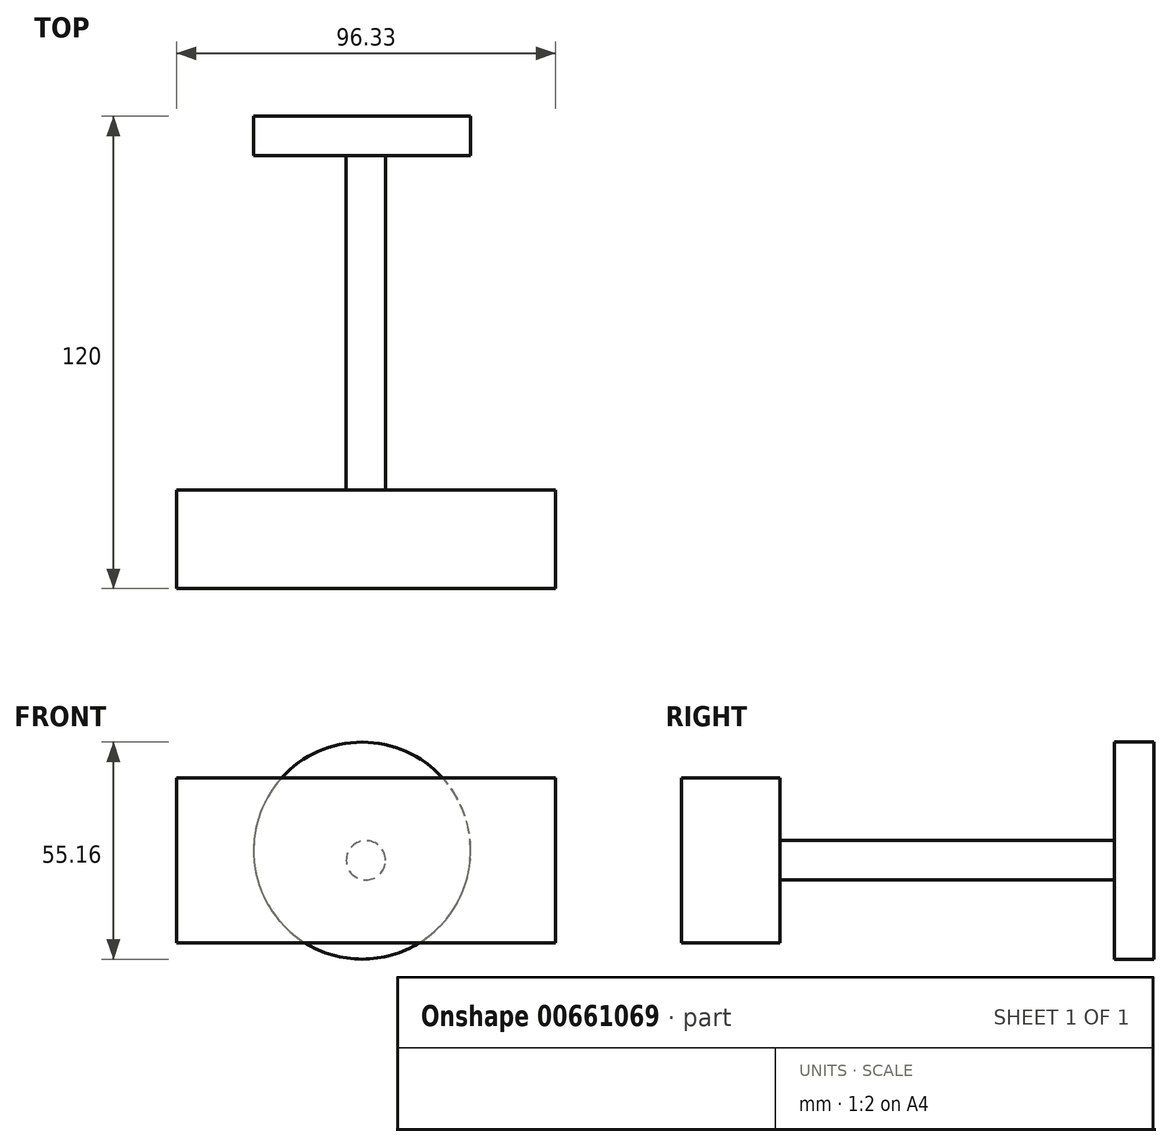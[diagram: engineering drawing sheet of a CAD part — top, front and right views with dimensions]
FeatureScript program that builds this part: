
annotation { "Feature Type Name" : "Feature", "Feature Type Description" : "" }
export const myFeature = defineFeature(function(context is Context, id is Id, definition is map)
    precondition{}
    {
        {
            var Q0;
            Q0=qCreatedBy(makeId("Front.planeOp"),FACE);
            var sketch = newSketch(context, id + "F0", { "sketchPlane" : qUnion([Q0])});
            skCircle(sketch, "E0", {"center": v(-28.35, 23.4) * mm, "radius": 27.58 * mm});
            skSolve(sketch);
        }
        {
            var Q0;
            Q0=makeQuery(id+"F0.imprint","IMPRINT",FACE,{"disambiguationData":[TD([[makeQuery(id+"F0.imprint","IMPRINT",EDGE,{"derivedFrom":sQuery(id+"F0.wireOp",EDGE,"E0")}),1.0]])]});
            extrude(context, id + "F1", {"entities" : qUnion([Q0]), "depth" : 10 * mm, "offsetDistance" : 25 * mm});
        }
        {
            var Q0;
            Q0=qCreatedBy(makeId("Front.planeOp"),FACE);
            var sketch = newSketch(context, id + "F2", { "sketchPlane" : qUnion([Q0])});
            skCircle(sketch, "E1", {"center": v(-27.38, 20.94) * mm, "radius": 5 * mm});
            skSolve(sketch);
        }
        {
            var Q0;
            Q0=makeQuery(id+"F2.imprint","IMPRINT",FACE,{"disambiguationData":[TD([[makeQuery(id+"F2.imprint","IMPRINT",EDGE,{"derivedFrom":sQuery(id+"F2.wireOp",EDGE,"E1")}),1.0]])]});
            extrude(context, id + "F3", {"entities" : qUnion([Q0]), "operationType" : NewBodyOperationType.ADD, "depth" : 95 * mm, "offsetDistance" : 25 * mm});
        }
        {
            var Q0;
            Q0=makeQuery(id+"F3.opExtrude","CAP_FACE",FACE,{"disambiguationData":[OSD([sQuery(id+"F2.wireOp",EDGE,"E1")])],"isStart":false});
            var sketch = newSketch(context, id + "F4", { "sketchPlane" : qUnion([Q0])});
            skLineSegment(sketch, "E2.bottom", {"start": v(-75.54, 0) * mm, "end": v(20.79, 0) * mm});
            skLineSegment(sketch, "E2.top", {"start": v(-75.54, 41.89) * mm, "end": v(20.79, 41.89) * mm});
            skLineSegment(sketch, "E2.left", {"start": v(-75.54, 0) * mm, "end": v(-75.54, 41.89) * mm});
            skLineSegment(sketch, "E2.right", {"start": v(20.79, 0) * mm, "end": v(20.79, 41.89) * mm});
            skPoint(sketch, "E2.middle", {"position": v(-27.38, 20.94) * mm});
            skSolve(sketch);
        }
        {
            var Q0;
            Q0 = qSketchRegion(id + "F4", true);
            extrude(context, id + "F5", {"entities" : qUnion([Q0]), "operationType" : NewBodyOperationType.ADD, "depth" : 25 * mm, "offsetDistance" : 25 * mm});
        }
    });
